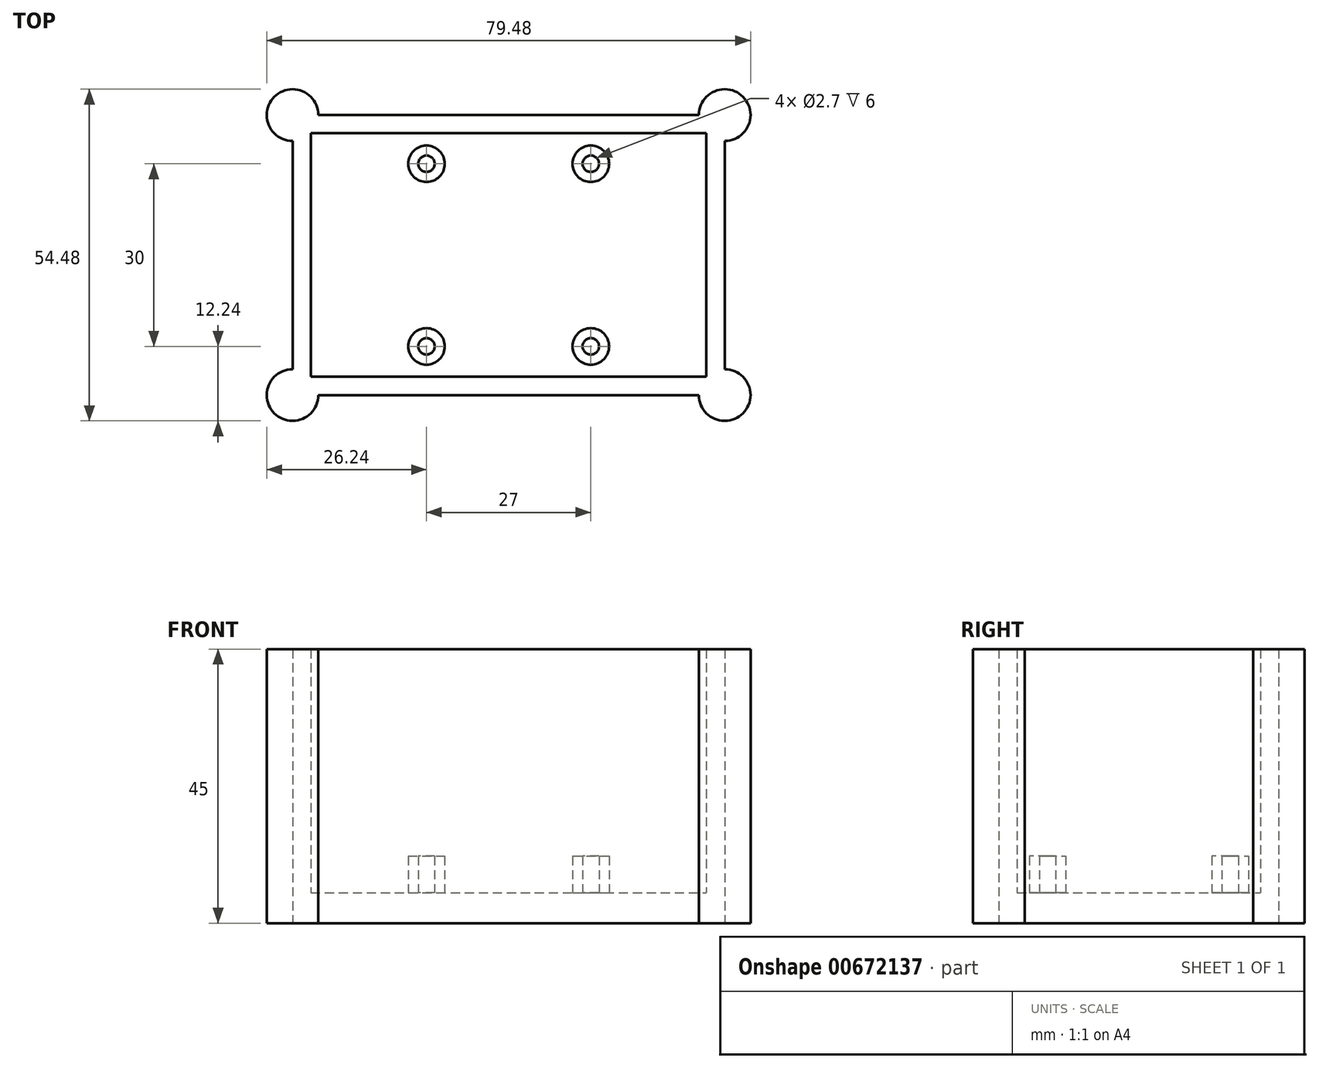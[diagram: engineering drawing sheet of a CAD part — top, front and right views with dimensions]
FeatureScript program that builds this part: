
annotation { "Feature Type Name" : "Feature", "Feature Type Description" : "" }
export const myFeature = defineFeature(function(context is Context, id is Id, definition is map)
    precondition{}
    {
        {
            var Q0;
            Q0=qCreatedBy(makeId("Top.planeOp"),FACE);
            var sketch = newSketch(context, id + "F0", { "sketchPlane" : qUnion([Q0])});
            skLineSegment(sketch, "E0.bottom", {"start": v(0, 0) * mm, "end": v(65, 0) * mm});
            skLineSegment(sketch, "E0.top", {"start": v(0, 40) * mm, "end": v(65, 40) * mm});
            skLineSegment(sketch, "E0.left", {"start": v(0, 0) * mm, "end": v(0, 40) * mm});
            skLineSegment(sketch, "E0.right", {"start": v(65, 0) * mm, "end": v(65, 40) * mm});
            skLineSegment(sketch, "E1.0", {"start": v(-3, 43) * mm, "end": v(68, 43) * mm});
            skLineSegment(sketch, "E1.1", {"start": v(-3, -3) * mm, "end": v(-3, 43) * mm});
            skLineSegment(sketch, "E1.2", {"start": v(-3, -3) * mm, "end": v(68, -3) * mm});
            skLineSegment(sketch, "E1.3", {"start": v(68, -3) * mm, "end": v(68, 43) * mm});
            skCircle(sketch, "E2", {"center": v(-3, 43) * mm, "radius": 4.24 * mm});
            skCircle(sketch, "E3", {"center": v(68, 43) * mm, "radius": 4.24 * mm});
            skCircle(sketch, "E4", {"center": v(-3, -3) * mm, "radius": 4.24 * mm});
            skCircle(sketch, "E5", {"center": v(68, -3) * mm, "radius": 4.24 * mm});
            skSolve(sketch);
        }
        {
            var Q0;
            {var subQ0=sQuery(id+"F0.wireOp",EDGE,"E1.1");var subQ1=sQuery(id+"F0.wireOp",EDGE,"E1.0");var subQ2=makeQuery(id+"F0.imprint","INTERSECT",VERTEX,{"derivedFrom":[subQ1,subQ0]});Q0=makeQuery(id+"F0.imprint","IMPRINT",FACE,{"disambiguationData":[TD([[makeQuery(id+"F0.imprint","IMPRINT",EDGE,{"disambiguationData":[TD([[subQ2,-1.0]])],"derivedFrom":subQ1}),1.0]])]});}
            var Q1;
            {var subQ0=sQuery(id+"F0.wireOp",EDGE,"E1.1");var subQ1=sQuery(id+"F0.wireOp",EDGE,"E1.0");var subQ2=makeQuery(id+"F0.imprint","INTERSECT",VERTEX,{"derivedFrom":[subQ1,subQ0]});Q1=makeQuery(id+"F0.imprint","IMPRINT",FACE,{"disambiguationData":[TD([[makeQuery(id+"F0.imprint","IMPRINT",EDGE,{"disambiguationData":[TD([[subQ2,-1.0]])],"derivedFrom":subQ1}),-1.0]])]});}
            var Q2;
            {var subQ0=sQuery(id+"F0.wireOp",EDGE,"E0.left");Q2=makeQuery(id+"F0.imprint","IMPRINT",FACE,{"disambiguationData":[TD([[makeQuery(id+"F0.imprint","IMPRINT",EDGE,{"derivedFrom":subQ0}),1.0]])]});}
            var Q3;
            {var subQ0=sQuery(id+"F0.wireOp",EDGE,"E0.top");Q3=makeQuery(id+"F0.imprint","IMPRINT",FACE,{"disambiguationData":[TD([[makeQuery(id+"F0.imprint","IMPRINT",EDGE,{"derivedFrom":subQ0}),1.0]])]});}
            var Q4;
            {var subQ0=sQuery(id+"F0.wireOp",EDGE,"E1.3");var subQ1=sQuery(id+"F0.wireOp",EDGE,"E1.0");var subQ2=makeQuery(id+"F0.imprint","INTERSECT",VERTEX,{"derivedFrom":[subQ1,subQ0]});Q4=makeQuery(id+"F0.imprint","IMPRINT",FACE,{"disambiguationData":[TD([[makeQuery(id+"F0.imprint","IMPRINT",EDGE,{"disambiguationData":[TD([[subQ2,1.0]])],"derivedFrom":subQ1}),1.0]])]});}
            var Q5;
            {var subQ0=sQuery(id+"F0.wireOp",EDGE,"E1.3");var subQ1=sQuery(id+"F0.wireOp",EDGE,"E1.0");var subQ2=makeQuery(id+"F0.imprint","INTERSECT",VERTEX,{"derivedFrom":[subQ1,subQ0]});Q5=makeQuery(id+"F0.imprint","IMPRINT",FACE,{"disambiguationData":[TD([[makeQuery(id+"F0.imprint","IMPRINT",EDGE,{"disambiguationData":[TD([[subQ2,1.0]])],"derivedFrom":subQ1}),-1.0]])]});}
            var Q6;
            {var subQ0=sQuery(id+"F0.wireOp",EDGE,"E1.3");var subQ1=sQuery(id+"F0.wireOp",EDGE,"E1.2");var subQ2=makeQuery(id+"F0.imprint","INTERSECT",VERTEX,{"derivedFrom":[subQ1,subQ0]});Q6=makeQuery(id+"F0.imprint","IMPRINT",FACE,{"disambiguationData":[TD([[makeQuery(id+"F0.imprint","IMPRINT",EDGE,{"disambiguationData":[TD([[subQ2,1.0]])],"derivedFrom":subQ1}),-1.0]])]});}
            var Q7;
            {var subQ0=sQuery(id+"F0.wireOp",EDGE,"E1.3");var subQ1=sQuery(id+"F0.wireOp",EDGE,"E1.2");var subQ2=makeQuery(id+"F0.imprint","INTERSECT",VERTEX,{"derivedFrom":[subQ1,subQ0]});Q7=makeQuery(id+"F0.imprint","IMPRINT",FACE,{"disambiguationData":[TD([[makeQuery(id+"F0.imprint","IMPRINT",EDGE,{"disambiguationData":[TD([[subQ2,1.0]])],"derivedFrom":subQ1}),1.0]])]});}
            var Q8;
            {var subQ0=sQuery(id+"F0.wireOp",EDGE,"E1.2");var subQ1=sQuery(id+"F0.wireOp",EDGE,"E1.1");var subQ2=makeQuery(id+"F0.imprint","INTERSECT",VERTEX,{"derivedFrom":[subQ1,subQ0]});Q8=makeQuery(id+"F0.imprint","IMPRINT",FACE,{"disambiguationData":[TD([[makeQuery(id+"F0.imprint","IMPRINT",EDGE,{"disambiguationData":[TD([[subQ2,-1.0]])],"derivedFrom":subQ1}),1.0]])]});}
            var Q9;
            {var subQ0=sQuery(id+"F0.wireOp",EDGE,"E1.2");var subQ1=sQuery(id+"F0.wireOp",EDGE,"E1.1");var subQ2=makeQuery(id+"F0.imprint","INTERSECT",VERTEX,{"derivedFrom":[subQ1,subQ0]});Q9=makeQuery(id+"F0.imprint","IMPRINT",FACE,{"disambiguationData":[TD([[makeQuery(id+"F0.imprint","IMPRINT",EDGE,{"disambiguationData":[TD([[subQ2,-1.0]])],"derivedFrom":subQ1}),-1.0]])]});}
            var Q10;
            {var subQ0=sQuery(id+"F0.wireOp",EDGE,"E0.bottom");Q10=makeQuery(id+"F0.imprint","IMPRINT",FACE,{"disambiguationData":[TD([[makeQuery(id+"F0.imprint","IMPRINT",EDGE,{"derivedFrom":subQ0}),-1.0]])]});}
            var Q11;
            {var subQ0=sQuery(id+"F0.wireOp",EDGE,"E0.right");Q11=makeQuery(id+"F0.imprint","IMPRINT",FACE,{"disambiguationData":[TD([[makeQuery(id+"F0.imprint","IMPRINT",EDGE,{"derivedFrom":subQ0}),-1.0]])]});}
            extrude(context, id + "F1", {"entities" : qUnion([Q0, Q1, Q2, Q3, Q4, Q5, Q6, Q7, Q8, Q9, Q10, Q11]), "depth" : 40 * mm, "offsetDistance" : 25 * mm});
        }
        {
            var Q0;
            Q0=makeQuery(id+"F1.opExtrude","CAP_FACE",FACE,{"disambiguationData":[OSD([sQuery(id+"F0.wireOp",EDGE,"E0.bottom"),sQuery(id+"F0.wireOp",EDGE,"E0.top"),sQuery(id+"F0.wireOp",EDGE,"E0.left"),sQuery(id+"F0.wireOp",EDGE,"E0.right"),sQuery(id+"F0.wireOp",EDGE,"E1.0"),sQuery(id+"F0.wireOp",EDGE,"E1.1"),sQuery(id+"F0.wireOp",EDGE,"E1.2"),sQuery(id+"F0.wireOp",EDGE,"E1.3"),sQuery(id+"F0.wireOp",EDGE,"E2"),sQuery(id+"F0.wireOp",EDGE,"E3"),sQuery(id+"F0.wireOp",EDGE,"E4"),sQuery(id+"F0.wireOp",EDGE,"E5")])],"isStart":true});
            var sketch = newSketch(context, id + "F2", { "sketchPlane" : qUnion([Q0])});
            skArc(sketch, "E6.0.0", {"start": v(-3, -38.76) * mm, "mid": v(-6, -46) * mm, "end": v(1.24, -43) * mm});
            skLineSegment(sketch, "E6.0.1", {"start": v(1.24, -43) * mm, "end": v(63.76, -43) * mm});
            skArc(sketch, "E6.0.2", {"start": v(63.76, -43) * mm, "mid": v(71, -46) * mm, "end": v(68, -38.76) * mm});
            skLineSegment(sketch, "E6.0.3", {"start": v(68, -38.76) * mm, "end": v(68, -1.24) * mm});
            skArc(sketch, "E6.0.4", {"start": v(68, -1.24) * mm, "mid": v(71, 6) * mm, "end": v(63.76, 3) * mm});
            skLineSegment(sketch, "E6.0.5", {"start": v(63.76, 3) * mm, "end": v(1.24, 3) * mm});
            skArc(sketch, "E6.0.6", {"start": v(1.24, 3) * mm, "mid": v(-6, 6) * mm, "end": v(-3, -1.24) * mm});
            skLineSegment(sketch, "E6.0.7", {"start": v(-3, -1.24) * mm, "end": v(-3, -38.76) * mm});
            skSolve(sketch);
        }
        {
            var Q0;
            Q0=makeQuery(id+"F2.imprint","IMPRINT",FACE,{"disambiguationData":[TD([[makeQuery(id+"F2.imprint","IMPRINT",EDGE,{"derivedFrom":sQuery(id+"F2.wireOp",EDGE,"E6.0.0")}),-1.0]])]});
            var Q1;
            Q1=makeQuery(id+"F2.imprint","IMPRINT",FACE,{"disambiguationData":[TD([[makeQuery(id+"F2.imprint","IMPRINT",EDGE,{"derivedFrom":makeQuery(id+"F1.opExtrude","CAP_EDGE",EDGE,{"disambiguationData":[OSD([sQuery(id+"F0.wireOp",EDGE,"E0.bottom")])],"isStart":true})}),-1.0]])]});
            extrude(context, id + "F3", {"entities" : qUnion([Q0, Q1]), "operationType" : NewBodyOperationType.ADD, "depth" : 5 * mm, "offsetDistance" : 25 * mm});
        }
        {
            var Q0;
            Q0=makeQuery(id+"F3.opExtrude","CAP_FACE",FACE,{"disambiguationData":[OSD([sQuery(id+"F2.wireOp",EDGE,"E6.0.0"),sQuery(id+"F2.wireOp",EDGE,"E6.0.1"),sQuery(id+"F2.wireOp",EDGE,"E6.0.2"),sQuery(id+"F2.wireOp",EDGE,"E6.0.3"),sQuery(id+"F2.wireOp",EDGE,"E6.0.4"),sQuery(id+"F2.wireOp",EDGE,"E6.0.5"),sQuery(id+"F2.wireOp",EDGE,"E6.0.6"),sQuery(id+"F2.wireOp",EDGE,"E6.0.7")])],"isStart":true});
            var sketch = newSketch(context, id + "F4", { "sketchPlane" : qUnion([Q0])});
            skLineSegment(sketch, "E7.bottom", {"start": v(19, 5) * mm, "end": v(46, 5) * mm});
            skLineSegment(sketch, "E7.top", {"start": v(19, 35) * mm, "end": v(46, 35) * mm});
            skLineSegment(sketch, "E7.left", {"start": v(19, 5) * mm, "end": v(19, 35) * mm});
            skLineSegment(sketch, "E7.right", {"start": v(46, 5) * mm, "end": v(46, 35) * mm});
            skLineSegment(sketch, "E8.0", {"start": v(0, 40) * mm, "end": v(65, 40) * mm});
            skArc(sketch, "E9.0.0", {"start": v(1.24, 43) * mm, "mid": v(-6, 46) * mm, "end": v(-3, 38.76) * mm});
            skLineSegment(sketch, "E9.0.1", {"start": v(-3, 38.76) * mm, "end": v(-3, 1.24) * mm});
            skArc(sketch, "E9.0.2", {"start": v(-3, 1.24) * mm, "mid": v(-6, -6) * mm, "end": v(1.24, -3) * mm});
            skLineSegment(sketch, "E9.0.3", {"start": v(1.24, -3) * mm, "end": v(63.76, -3) * mm});
            skArc(sketch, "E9.0.4", {"start": v(63.76, -3) * mm, "mid": v(71, -6) * mm, "end": v(68, 1.24) * mm});
            skLineSegment(sketch, "E9.0.5", {"start": v(68, 1.24) * mm, "end": v(68, 38.76) * mm});
            skArc(sketch, "E9.0.6", {"start": v(68, 38.76) * mm, "mid": v(71, 46) * mm, "end": v(63.76, 43) * mm});
            skLineSegment(sketch, "E9.0.7", {"start": v(63.76, 43) * mm, "end": v(1.24, 43) * mm});
            skLineSegment(sketch, "E10", {"start": v(32.5, 40) * mm, "end": v(32.5, 35) * mm});
            skLineSegment(sketch, "E11", {"start": v(0, 20) * mm, "end": v(19, 20) * mm});
            skCircle(sketch, "E12", {"center": v(19, 35) * mm, "radius": 3 * mm});
            skCircle(sketch, "E13", {"center": v(46, 35) * mm, "radius": 3 * mm});
            skCircle(sketch, "E14", {"center": v(19, 5) * mm, "radius": 3 * mm});
            skCircle(sketch, "E15", {"center": v(46, 5) * mm, "radius": 3 * mm});
            skCircle(sketch, "E16", {"center": v(19, 35) * mm, "radius": 1.35 * mm});
            skCircle(sketch, "E17", {"center": v(46, 35) * mm, "radius": 1.35 * mm});
            skCircle(sketch, "E18", {"center": v(19, 5) * mm, "radius": 1.35 * mm});
            skCircle(sketch, "E19", {"center": v(46, 5) * mm, "radius": 1.35 * mm});
            skSolve(sketch);
        }
        {
            var Q0;
            {var subQ0=sQuery(id+"F4.wireOp",EDGE,"E16");var subQ1=sQuery(id+"F4.wireOp",EDGE,"E7.top");var subQ2=makeQuery(id+"F4.imprint","INTERSECT",VERTEX,{"derivedFrom":[subQ1,subQ0]});Q0=makeQuery(id+"F4.imprint","IMPRINT",FACE,{"disambiguationData":[TD([[makeQuery(id+"F4.imprint","IMPRINT",EDGE,{"disambiguationData":[TD([[subQ2,-1.0]])],"derivedFrom":subQ1}),1.0]])]});}
            var Q1;
            {var subQ0=sQuery(id+"F4.wireOp",EDGE,"E16");var subQ1=sQuery(id+"F4.wireOp",EDGE,"E7.top");var subQ2=makeQuery(id+"F4.imprint","INTERSECT",VERTEX,{"derivedFrom":[subQ1,subQ0]});Q1=makeQuery(id+"F4.imprint","IMPRINT",FACE,{"disambiguationData":[TD([[makeQuery(id+"F4.imprint","IMPRINT",EDGE,{"disambiguationData":[TD([[subQ2,-1.0]])],"derivedFrom":subQ1}),-1.0]])]});}
            var Q2;
            {var subQ0=sQuery(id+"F4.wireOp",EDGE,"E13");var subQ1=sQuery(id+"F4.wireOp",EDGE,"E7.top");var subQ2=makeQuery(id+"F4.imprint","INTERSECT",VERTEX,{"derivedFrom":[subQ1,subQ0]});Q2=makeQuery(id+"F4.imprint","IMPRINT",FACE,{"disambiguationData":[TD([[makeQuery(id+"F4.imprint","IMPRINT",EDGE,{"disambiguationData":[TD([[subQ2,-1.0]])],"derivedFrom":subQ1}),1.0]])]});}
            var Q3;
            {var subQ0=sQuery(id+"F4.wireOp",EDGE,"E13");var subQ1=sQuery(id+"F4.wireOp",EDGE,"E7.top");var subQ2=makeQuery(id+"F4.imprint","INTERSECT",VERTEX,{"derivedFrom":[subQ1,subQ0]});Q3=makeQuery(id+"F4.imprint","IMPRINT",FACE,{"disambiguationData":[TD([[makeQuery(id+"F4.imprint","IMPRINT",EDGE,{"disambiguationData":[TD([[subQ2,-1.0]])],"derivedFrom":subQ1}),-1.0]])]});}
            var Q4;
            {var subQ0=sQuery(id+"F4.wireOp",EDGE,"E18");var subQ1=sQuery(id+"F4.wireOp",EDGE,"E7.bottom");var subQ2=makeQuery(id+"F4.imprint","INTERSECT",VERTEX,{"derivedFrom":[subQ1,subQ0]});Q4=makeQuery(id+"F4.imprint","IMPRINT",FACE,{"disambiguationData":[TD([[makeQuery(id+"F4.imprint","IMPRINT",EDGE,{"disambiguationData":[TD([[subQ2,-1.0]])],"derivedFrom":subQ1}),1.0]])]});}
            var Q5;
            {var subQ0=sQuery(id+"F4.wireOp",EDGE,"E18");var subQ1=sQuery(id+"F4.wireOp",EDGE,"E7.bottom");var subQ2=makeQuery(id+"F4.imprint","INTERSECT",VERTEX,{"derivedFrom":[subQ1,subQ0]});Q5=makeQuery(id+"F4.imprint","IMPRINT",FACE,{"disambiguationData":[TD([[makeQuery(id+"F4.imprint","IMPRINT",EDGE,{"disambiguationData":[TD([[subQ2,-1.0]])],"derivedFrom":subQ1}),-1.0]])]});}
            var Q6;
            {var subQ0=sQuery(id+"F4.wireOp",EDGE,"E15");var subQ1=sQuery(id+"F4.wireOp",EDGE,"E7.bottom");var subQ2=makeQuery(id+"F4.imprint","INTERSECT",VERTEX,{"derivedFrom":[subQ1,subQ0]});Q6=makeQuery(id+"F4.imprint","IMPRINT",FACE,{"disambiguationData":[TD([[makeQuery(id+"F4.imprint","IMPRINT",EDGE,{"disambiguationData":[TD([[subQ2,-1.0]])],"derivedFrom":subQ1}),1.0]])]});}
            var Q7;
            {var subQ0=sQuery(id+"F4.wireOp",EDGE,"E15");var subQ1=sQuery(id+"F4.wireOp",EDGE,"E7.bottom");var subQ2=makeQuery(id+"F4.imprint","INTERSECT",VERTEX,{"derivedFrom":[subQ1,subQ0]});Q7=makeQuery(id+"F4.imprint","IMPRINT",FACE,{"disambiguationData":[TD([[makeQuery(id+"F4.imprint","IMPRINT",EDGE,{"disambiguationData":[TD([[subQ2,-1.0]])],"derivedFrom":subQ1}),-1.0]])]});}
            extrude(context, id + "F5", {"entities" : qUnion([Q0, Q1, Q2, Q3, Q4, Q5, Q6, Q7]), "operationType" : NewBodyOperationType.ADD, "depth" : 6 * mm, "offsetDistance" : 25 * mm});
        }
    });
